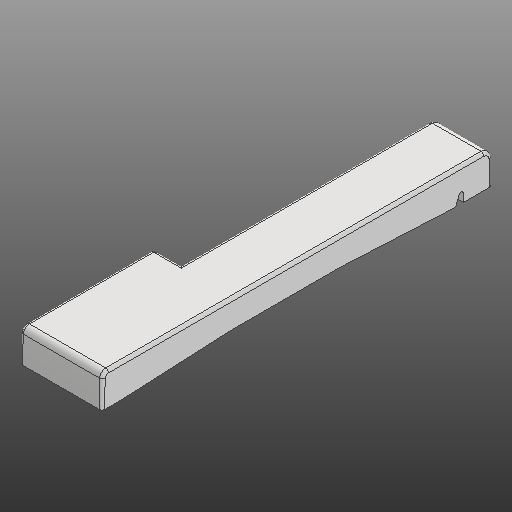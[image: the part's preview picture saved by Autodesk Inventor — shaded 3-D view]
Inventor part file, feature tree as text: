
AUTODESK INVENTOR PART (.ipt)
format: ipt  version: 2020 (Build 240168000, 168)  size: 320,000 bytes
history: native  units: in
note: dims shown in document units (in); Inventor stores cm internally (conversion verified against a paired STEP export)
features: extrude x4, other x3, fillet x2
ambient origin geometry x8: Origin, YZ Plane, XZ Plane, XY Plane, X Axis, Y Axis, Z Axis, Center Point
bodies: Solid1 (feature_tree)
feature tree (9):
  other  "Slot Start Plane"
  other  "Key Profile"
  extrude  "Upper (u)"  TaperAngle=0.0deg  [1 undecoded]
  extrude  "Lower (d)"  TaperAngle=0.0deg  [1 undecoded]
  extrude  "Protrusion Cutout"  Depth=0.0591in
  fillet  "Front Fillet"  Radius=0.1374in
  extrude  "Slot"  [1 undecoded]
  fillet  "Edge Softening"  Radius=0.0787in
  other  "Slot Sketch"
note: 3 required parameter values undecoded (feature->parameter linkage not recoverable at this tier; creation-order binding heuristic only, values carry confidence <= 0.55)
